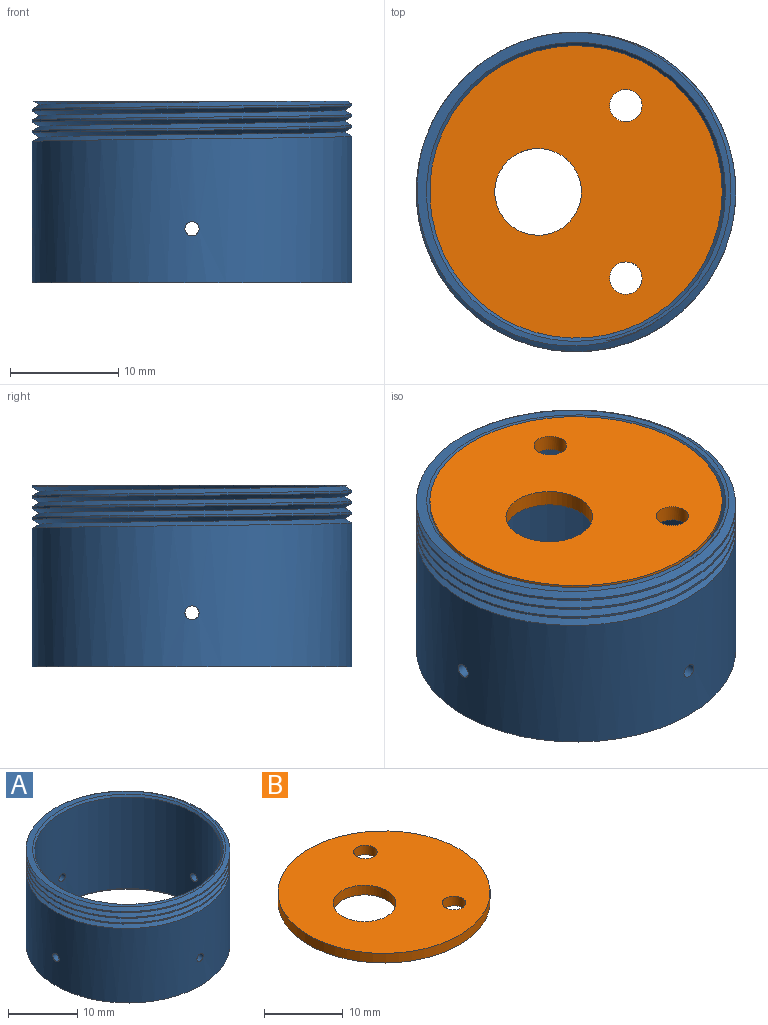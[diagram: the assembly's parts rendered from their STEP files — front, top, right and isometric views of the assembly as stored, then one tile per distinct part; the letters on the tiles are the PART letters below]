
ASSEMBLY  parts=2 mates=1
PART A: 17 faces, bbox 30x34.6x17.9 mm
  f0: cylinder r=14.75mm len=29.5mm, axis (0,0,-1), area 1204.1mm2, adj f1,f7,f8,f9,f13,f14,f15,f16
  f1: cylinder r=14.75mm len=29.5mm, axis (0,0,-1), area 18.5mm2, adj f0,f2,f9,f10
  f2: cylinder r=14.75mm len=29.5mm, axis (0,0,-1), area 18.5mm2, adj f1,f3,f9,f10
  f3: cylinder r=14.75mm len=29.5mm, axis (0,0,-1), area 18.5mm2, adj f2,f4,f9,f10
  f4: cylinder r=14.75mm len=28.74mm, axis (0,0,-1), area 6.5mm2, adj f3,f6,f9,f10
  f5: cylinder r=13.5mm len=27mm, axis (0,0,-1), area 1368.8mm2, adj f11,f12,f13,f14,f15,f16
  f6: plane 29.52x29.52mm, normal (0,0,1), area 59.9mm2, adj f4,f9,f10,f11
  f7: plane 29.5x29.5mm, normal (0,0,-1), area 85.2mm2, adj f0,f12
  f8: plane 0.8x0.69mm, normal (0,1,0), area 0.3mm2, adj f0,f9,f10
  f9: bspline ~34.06x29.5mm, area 293.4mm2, adj f0,f1,f2,f3,f4,f6,f8,f10
  f10: bspline ~34.06x29.5mm, area 264mm2, adj f1,f2,f3,f4,f6,f8,f9
  f11: cone r=13.5mm half-angle=45deg, axis (0,0,1), area 36.4mm2, adj f5,f6
  f12: cone r=13.8mm half-angle=45deg, axis (0,0,-1), area 36.4mm2, adj f5,f7
  f13: cylinder r=0.65mm len=1.3mm, axis (0,-1,0), area 5.1mm2, adj f0,f5
  f14: cylinder r=0.65mm len=1.3mm, axis (0,-1,0), area 5.1mm2, adj f0,f5
  f15: cylinder r=0.65mm len=1.3mm, axis (1,0,0), area 5.1mm2, adj f0,f5
  f16: cylinder r=0.65mm len=1.3mm, axis (1,0,0), area 5.1mm2, adj f0,f5
PART B: 6 faces, bbox 27x27x1.5 mm
  f0: cylinder r=13.5mm len=27mm, axis (0,0,-1), area 127.2mm2, adj f2,f3
  f1: cylinder r=4mm len=8mm, axis (0,0,-1), area 37.7mm2, adj f2,f3
  f2: plane 27x27mm, normal (0,0,1), area 508.2mm2, adj f0,f1,f4,f5
  f3: plane 27x27mm, normal (0,0,-1), area 508.2mm2, adj f0,f1,f4,f5
  f4: cylinder r=1.5mm len=3mm, axis (0,0,-1), area 14.1mm2, adj f2,f3
  f5: cylinder r=1.5mm len=3mm, axis (0,0,-1), area 14.1mm2, adj f2,f3
PLACE A t=(2.44,-1.01,-4.44)mm
PLACE B t=(2.44,-1.31,10.86)mm
MATE fastened B.f0 <-> A.f0  axis (0,0,1) through (2.44,-1.01,12.36)mm
